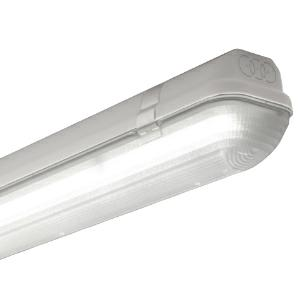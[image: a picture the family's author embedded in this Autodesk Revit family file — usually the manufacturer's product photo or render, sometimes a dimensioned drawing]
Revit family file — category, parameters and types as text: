
# Revit family: 3f_filippi_-_3f_linda_3f_filippi_-_58585_-_3f_linda_led_1x24w-830_l1270
name_source: partatom
category: Lighting Fixtures
units: mm (PartAtom-declared; Revit-internal decimal feet)

## family parameters
Cut with Voids When Loaded = No
Host = Face
Light Source = No
Part Type = Normal
Room Calculation Point = No
Round Connector Dimension = Use Diameter
Shared = No

## types (1)
- 3F Filippi - 3F Linda (1 x LED, 3862 lm, 28 W, 3000 K)
    Apparent Load = 28 VA
    Approval mark = CE
    CIE Flux Codes = 44 77 94 97 100
    Color Rendering = 80
    Color Temperature = 3000 K
    Control Gear = Electronic ballast
    Default Elevation = 1800 mm
    Description = ILLUMINOTECHNICAL
Luminous efficiency 100% (DLOR 97%, ULOR 3%).
Initial luminous flux of the luminaire 3862 lm.
Controlled symmetric distribution.
Installation Interdistance Transv.D = 1.77 x hu - Long.D = 1.17 x hu.
Tabular UGR (CIE 117 - 4H-8H; S=0.25H; 70/50/20): RUG 21.8 - 22.7.
Beam angle: 109° - 64°.
Luminous efficacy 138 lm/W.
Lifetime (L93/B10): 30000 h. (tq+25°C)
Lifetime (L90/B10): 50000 h. (tq+25°C)
Lifetime (L85/B10): 80000 h. (tq+25°C)
Lifetime (L80/B10): 100000 h. (tq+25°C)
Lifetime (L85/B10): 50000 h. (tq+35°C)
Sudden decreased luminous flux after 50000 hours: 0% (C0).
Photobiological safety in compliance with IEC/TR 62778: RG0 risk exempt, (IEC 62471).
In compliance with IEC/EN 62722-2-1 - IEC/EN 62717 standards.

SOURCE
Linear LED module 24W/830.
Energy efficiency class (UE 2019/2020 - UE 2019/2015): D.
CIE 13.3 Colour rendering index: CRI >80 (R9 <50%).
IES TM-30 Fidelity Index: Rf = 84 Rg = 95.
CCT nominal colour temperature 3000 K.
Colour initial tolerance (MacAdam): SDCM 3.

MECHANICAL
Self-extinguishing V2 polycarbonate housing, injection moulded, RAL 7035 grey.
Ecologic anti-aging injected sealing gasket.
Diffuser in self-extinguishing V2 polycarbonate, photo-engraved interior, UV stabilised, injection moulded with smooth outer surface, tamper-proof opening.
Gear-holder reflector in hot-dip galvanised steel, painted with white polyester base.
Snug fit safety snap-lock clips for diffuser mounting in stainless steel, screwdriver opening.
Fixing brackets in stainless steel.
Possibility for technicians to access the interior of the luminaire.
Luminaire with limited surface temperature. - D - (EN 60598-2-24)
Dimensions: 1270x100 mm, height 100 mm. Weight 2.089 kg.
IP66 protection degree.
Mechanical strength to impacts IK10 (20 joule).
Glow-wire test resistance 850°C.

ELECTRICAL
Halogen Free electronic wiring 230V-50/60Hz, power factor 0.90, THD <25%, constant output current, SELV, class I, 1 driver.
Power of the luminaire 28 W.
ENEC - CE.
SAFE FLICKER: PstLM=<1 and SVM=<0.4 (IEC TR 61547-1 and IEC TR 63158), to ensure a more comfortable and safe light.
Luminaire compliant with EN 60598-2-22 for power supply from a centralised emergency system CPSS (Central Power Supply System), not incorporated in the luminaire - high risk areas excluded. The default power and flux are 100% in AC and 100% in DC.
Ambient temperature from -20°C to +35°C.
Temperature class T6 max 85°C.
Relative humidity UR: <85%.

INSTALLATION
Ceiling / Suspended / Wall.
All accessories dedicated to this product are available on the Catalog and on our website www.3F-Filippi.com.

APPLICATIONS
Suitable product for food production plants (HACCP), IFS (Food Version 6), BRC (GSFS Food Version 7).
Dry, dusty indoor environments, subject to occasional water splashes.
Virtually shatterproof polycarbonate compatibly with the fumes / atmospheres that compromise the elasticity of plastic materials.
Not suitable for installation on surfaces subject to important vibrations, exposed to weather conditions, on ropes or poles.
Suitable for illumination of public car parks and parking grounds referred to DIN 67528:2018-04.

WARNING
Fixture not suitable for cold stores with an ambient temperature <0°C and/or relative humidity >85%.
Luminaire designed for disposal/recycling at end-of-life.
Replaceable (LED only) light source by a professional. Replaceable control gear by a professional.
    Height = 100 mm  [stored 0.328084 ft]
    Lamp = 1 x LED
    Lamp Light Flux = 3862 lm
    Lamp Power = 28 W
    Lamp count = 1
    Length = 1270 mm
    Lifetime = 50000 h
    Luminous efficacy = 138 lm/W
    Manufacturer = 3F Filippi
    ModVariant = No
    Model = 3F Filippi - 58585 - 3F Linda LED 1x24W-830 L1270
    Mounting Place = Ceiling
    Mounting Type = Pendant
    Number of Poles = 1
    OnlyDefault = Yes
    Power Factor = 1
    Product Name = 3F Filippi - 3F Linda
    Product group = pendant luminaire
    ProductGroupID = 9
    Protection Class = Protection class I
    Protection Degree = IP 66
    RLX_Detail_Level = 1
    RLX_Emergency_Light_Flux = 0 lm
    RLX_Emergency_Type = 0
    RLX_Emergency_Type_DB = No
    RlxData = <blob elided: 70669 chars, md5=d8dee14d>
    Socket = socket
    Standby Power = 0 W
    System Light Flux = 3862 lm
    System Power = 28 W
    Type Comments = Product without accessories
    Type Image = 3ffilippi_3f_linda_led.jpg
    URL = http://relux.com
    VarID = ---
    Voltage = 0 V
    Weight = 0.00 kg
    Width = 100 mm  [stored 0.328084 ft]

note: [stored X ft] marks values corroborated as IEEE doubles in the binary element streams (Revit-internal decimal feet)

## geometry (parser evidence)
native form markers: Blend x4, Sweep x10
no freeform markers — native parametric forms only
